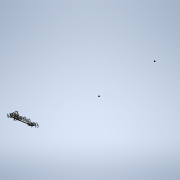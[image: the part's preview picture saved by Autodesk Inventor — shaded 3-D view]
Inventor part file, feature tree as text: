
AUTODESK INVENTOR PART (.ipt)
format: ipt  version: 2020.3 (Build 243373000, 373)  size: 238,592 bytes
history: native  units: mm
features: fillet x5, hole x3, sketch x2, extrude x2, chamfer x1
ambient origin geometry x8: Origin, YZ Plane, XZ Plane, XY Plane, X Axis, Y Axis, Z Axis, Center Point
bodies: Solid1 (feature_tree)
feature tree (13):
  sketch  "Sketch1"  dims[d4=6.0mm d5=23.0mm]
  extrude  "Extrusion1"  Depth=23.0mm
  chamfer  "Chamfer1"  Distance=5.0mm
  fillet  "Fillet1"  Radius=7.0mm
  fillet  "Fillet2"  Radius=5.0mm
  fillet  "Fillet3"  Radius=4.0mm
  fillet  "Fillet4"  Radius=20.0mm
  hole  "Hole3"  [1 undecoded]
  hole  "Hole4"  [1 undecoded]
  extrude  "Extrusion3"  Depth=5.0mm
  fillet  "Fillet6"  Radius=6.0mm
  hole  "Hole5"  [1 undecoded]
  sketch  "Sketch2"  dims[d6=12.2mm d7=5.0mm d15=7.0mm d17=5.0mm d18=4.0mm d21=20.0mm d23=80.0mm d24=15.0mm d29=29.670597mm d30=6.0mm d31=10.0mm d33=6.0mm d34=0.0mm d37=2.5mm d38=2.0mm d39=45.0deg d40=3.0mm d41=3.0mm d42=2.0mm d43=4.0mm d44=3.0mm d45=4.0mm d50=13.0mm d51=12.0mm d52=22.68928mm d53=16.057029mm d61=0.5mm d69=2.2mm d70=6.0mm d71=4.0mm d72=2.0mm d73=90.0deg d74=5.0mm d75=20.594885mm d76=2.2mm d77=6.0mm d78=4.0mm d79=2.0mm d80=90.0deg d81=5.0mm d82=20.594885mm d83=20.92mm d84=0.0mm d86=2.0mm d87=6.0mm d88=2.0mm d89=6.0mm d90=4.0mm d91=2.0mm d92=90.0deg d93=5.0mm d94=20.594885mm d95=2.7mm]
note: 3 required parameter values undecoded (feature->parameter linkage not recoverable at this tier; creation-order binding heuristic only, values carry confidence <= 0.55)
